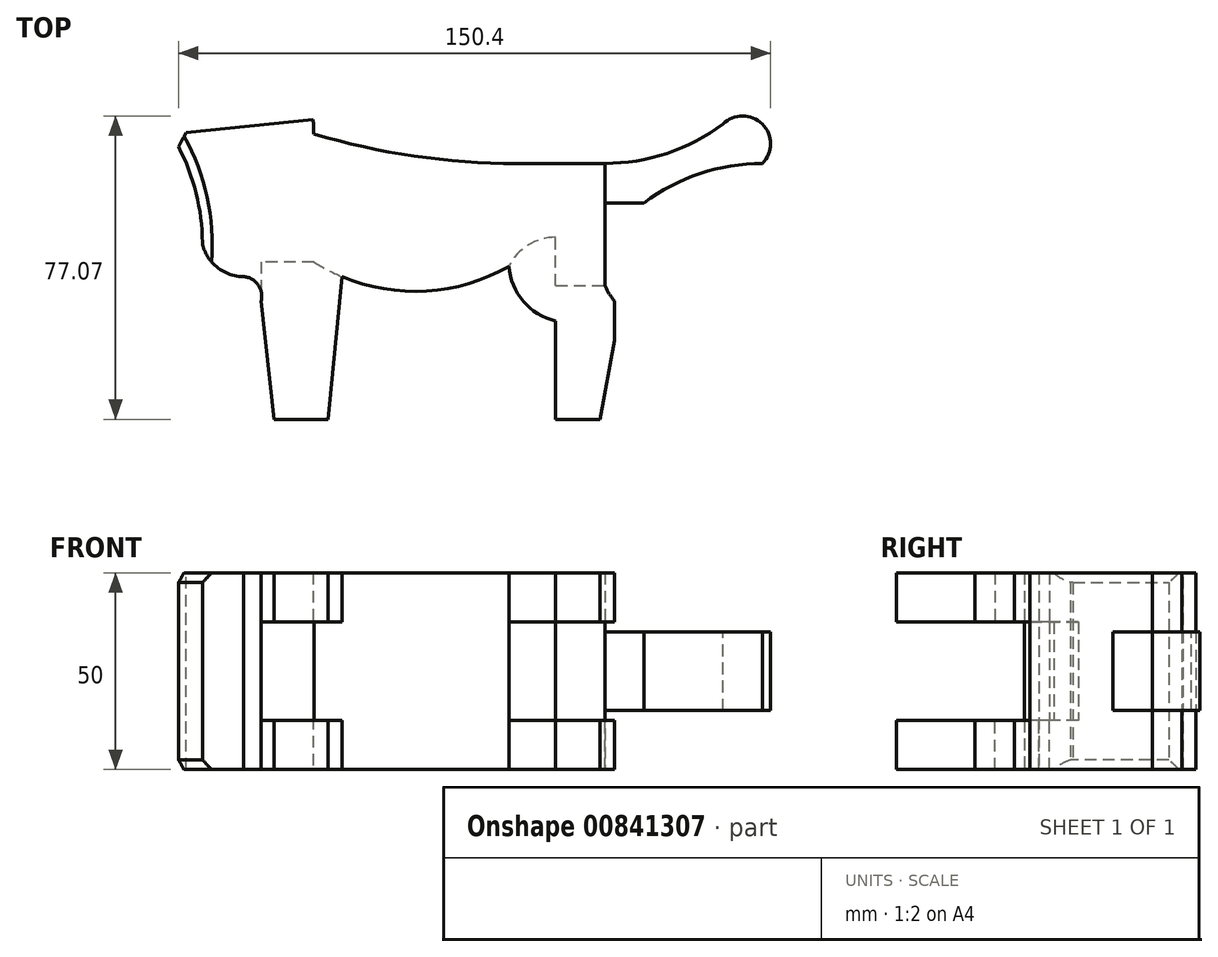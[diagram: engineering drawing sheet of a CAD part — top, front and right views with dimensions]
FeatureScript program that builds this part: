
annotation { "Feature Type Name" : "Feature", "Feature Type Description" : "" }
export const myFeature = defineFeature(function(context is Context, id is Id, definition is map)
    precondition{}
    {
        {
            var Q0;
            Q0=qCreatedBy(makeId("Top.planeOp"),FACE);
            var sketch = newSketch(context, id + "F0", { "sketchPlane" : qUnion([Q0])});
            skLineSegment(sketch, "E0.bottom", {"start": v(-56.24, 60.08) * mm, "end": v(-42.86, 60.08) * mm, "construction": true});
            skLineSegment(sketch, "E0.top", {"start": v(-56.24, 20.08) * mm, "end": v(-49.55, 20.08) * mm, "construction": true});
            skLineSegment(sketch, "E0.left", {"start": v(-56.24, 60.08) * mm, "end": v(-56.24, 27.58) * mm, "construction": true});
            skLineSegment(sketch, "E1", {"start": v(-42.86, 60.08) * mm, "end": v(-42.86, 27.58) * mm, "construction": true});
            skLineSegment(sketch, "E2", {"start": v(8.57, 60.08) * mm, "end": v(8.57, 52.58) * mm, "construction": true});
            skPoint(sketch, "E3", {"position": v(8.57, 52.58) * mm});
            skLineSegment(sketch, "E4", {"start": v(8.57, 52.58) * mm, "end": v(-42.86, 52.58) * mm, "construction": true});
            skArc(sketch, "E5", {"start": v(-42.86, 60.08) * mm, "mid": v(-17.42, 54.46) * mm, "end": v(8.57, 52.58) * mm});
            skPoint(sketch, "E6", {"position": v(8.57, 27.58) * mm});
            skArc(sketch, "E7", {"start": v(-42.86, 27.58) * mm, "mid": v(-17.15, 20.08) * mm, "end": v(8.57, 27.58) * mm});
            skPoint(sketch, "E8", {"position": v(-17.15, 20.08) * mm});
            skLineSegment(sketch, "E9.bottom", {"start": v(8.57, 52.58) * mm, "end": v(18.57, 52.58) * mm});
            skLineSegment(sketch, "E9.top", {"start": v(8.57, 27.58) * mm, "end": v(18.57, 27.58) * mm, "construction": true});
            skLineSegment(sketch, "E9.left", {"start": v(8.57, 52.58) * mm, "end": v(8.57, 27.58) * mm, "construction": true});
            skLineSegment(sketch, "E9.right", {"start": v(18.57, 52.58) * mm, "end": v(18.57, 40.08) * mm});
            skPoint(sketch, "E10", {"position": v(18.57, 40.08) * mm});
            skLineSegment(sketch, "E11", {"start": v(18.57, 40.08) * mm, "end": v(58.57, 40.08) * mm, "construction": true});
            skLineSegment(sketch, "E12", {"start": v(18.57, 52.58) * mm, "end": v(58.57, 52.58) * mm, "construction": true});
            skPoint(sketch, "E13", {"position": v(58.57, 60.08) * mm});
            skLineSegment(sketch, "E14", {"start": v(8.57, 27.58) * mm, "end": v(8.57, 20.08) * mm, "construction": true});
            skLineSegment(sketch, "E15.top", {"start": v(8.57, -12.42) * mm, "end": v(18.57, -12.42) * mm, "construction": true});
            skLineSegment(sketch, "E15.left", {"start": v(8.57, 27.58) * mm, "end": v(8.57, -12.42) * mm, "construction": true});
            skLineSegment(sketch, "E15.right", {"start": v(33.57, 27.58) * mm, "end": v(33.57, 17.58) * mm, "construction": true});
            skLineSegment(sketch, "E16", {"start": v(33.57, 7.58) * mm, "end": v(33.57, -12.42) * mm, "construction": true});
            skLineSegment(sketch, "E17", {"start": v(18.57, 40.08) * mm, "end": v(18.57, 33.83) * mm});
            skLineSegment(sketch, "E18", {"start": v(18.57, 27.58) * mm, "end": v(18.57, 27.58) * mm});
            skLineSegment(sketch, "E19", {"start": v(18.57, 27.58) * mm, "end": v(26.07, 27.58) * mm, "construction": true});
            skLineSegment(sketch, "E20", {"start": v(26.07, 27.58) * mm, "end": v(33.57, 27.58) * mm, "construction": true});
            skArc(sketch, "E21", {"start": v(29.82, 27.58) * mm, "mid": v(25, 32.16) * mm, "end": v(18.57, 33.83) * mm});
            skLineSegment(sketch, "E22", {"start": v(18.57, 27.58) * mm, "end": v(18.57, 12.58) * mm, "construction": true});
            skLineSegment(sketch, "E23", {"start": v(29.82, 27.58) * mm, "end": v(29.82, -12.42) * mm, "construction": true});
            skArc(sketch, "E24", {"start": v(29.82, 27.58) * mm, "mid": v(30.8, 22.24) * mm, "end": v(33.57, 17.58) * mm});
            skLineSegment(sketch, "E25", {"start": v(33.57, 17.58) * mm, "end": v(33.57, 7.58) * mm});
            skLineSegment(sketch, "E26", {"start": v(29.82, -12.42) * mm, "end": v(33.57, 7.58) * mm});
            skPoint(sketch, "E27.orphan", {"position": v(18.57, 33.83) * mm});
            skLineSegment(sketch, "E28", {"start": v(18.57, 33.83) * mm, "end": v(18.57, 27.58) * mm, "construction": true});
            skArc(sketch, "E29", {"start": v(18.57, 33.83) * mm, "mid": v(11.57, 31.83) * mm, "end": v(6.69, 26.44) * mm});
            skLineSegment(sketch, "E30", {"start": v(33.57, 12.58) * mm, "end": v(8.57, 12.58) * mm, "construction": true});
            skArc(sketch, "E31", {"start": v(6.69, 26.44) * mm, "mid": v(10.35, 17.56) * mm, "end": v(18.57, 12.58) * mm});
            skLineSegment(sketch, "E32", {"start": v(18.57, -12.42) * mm, "end": v(33.57, -12.42) * mm});
            skLineSegment(sketch, "E33", {"start": v(18.57, 12.58) * mm, "end": v(18.57, -12.42) * mm});
            skLineSegment(sketch, "E34", {"start": v(-42.86, 27.58) * mm, "end": v(-42.86, 20.08) * mm});
            skLineSegment(sketch, "E35", {"start": v(-42.86, 23.83) * mm, "end": v(-35.71, 23.83) * mm, "construction": true});
            skPoint(sketch, "E36.oppositeSnap0", {"position": v(13.57, -12.42) * mm});
            skLineSegment(sketch, "E36.bottom", {"start": v(-35.71, 23.83) * mm, "end": v(-60.71, 23.83) * mm, "construction": true});
            skLineSegment(sketch, "E36.top", {"start": v(-35.71, -12.42) * mm, "end": v(-39.29, -12.42) * mm, "construction": true});
            skLineSegment(sketch, "E36.left", {"start": v(-35.71, 23.83) * mm, "end": v(-35.71, -12.42) * mm, "construction": true});
            skLineSegment(sketch, "E36.right", {"start": v(-60.71, 23.83) * mm, "end": v(-60.71, -12.42) * mm, "construction": true});
            skLineSegment(sketch, "E37", {"start": v(-35.71, 23.83) * mm, "end": v(-39.29, -12.42) * mm});
            skPoint(sketch, "E37.endSnap0", {"position": v(-39.29, 23.83) * mm});
            skArc(sketch, "E38", {"start": v(-71.18, 32.16) * mm, "mid": v(-67.4, 26.17) * mm, "end": v(-60.71, 23.83) * mm});
            skPoint(sketch, "E38.startSnap0", {"position": v(25, 32.16) * mm});
            skArc(sketch, "E39", {"start": v(-56.24, 17.58) * mm, "mid": v(-57.02, 21.75) * mm, "end": v(-60.71, 23.83) * mm});
            skLineSegment(sketch, "E40", {"start": v(-49.55, 20.08) * mm, "end": v(-42.86, 20.08) * mm, "construction": true});
            skLineSegment(sketch, "E41", {"start": v(-56.24, 17.58) * mm, "end": v(-52.9, -12.42) * mm});
            skPoint(sketch, "E41.endSnap0", {"position": v(-52.9, 20.08) * mm});
            skLineSegment(sketch, "E42", {"start": v(-52.9, -12.42) * mm, "end": v(-60.71, -12.42) * mm, "construction": true});
            skLineSegment(sketch, "E43", {"start": v(-39.29, -12.42) * mm, "end": v(-52.9, -12.42) * mm});
            skLineSegment(sketch, "E44", {"start": v(-71.18, 32.16) * mm, "end": v(-71.18, 60.08) * mm, "construction": true});
            skArc(sketch, "E45", {"start": v(-71.18, 32.16) * mm, "mid": v(-73.2, 46.67) * mm, "end": v(-79.13, 60.08) * mm});
            skLineSegment(sketch, "E46.bottom", {"start": v(-42.86, 60.08) * mm, "end": v(-96.35, 60.08) * mm});
            skLineSegment(sketch, "E46.top", {"start": v(-42.86, 78.17) * mm, "end": v(-96.35, 78.17) * mm});
            skLineSegment(sketch, "E46.left", {"start": v(-42.86, 60.08) * mm, "end": v(-42.86, 78.17) * mm});
            skLineSegment(sketch, "E46.right", {"start": v(-96.35, 60.08) * mm, "end": v(-96.35, 78.17) * mm});
            skLineSegment(sketch, "E47", {"start": v(-42.86, 27.58) * mm, "end": v(-56.24, 27.58) * mm});
            skLineSegment(sketch, "E48", {"start": v(-56.24, 27.58) * mm, "end": v(-56.24, 20.08) * mm});
            skSolve(sketch);
        }
        {
            var Q0;
            {var subQ2=sQuery(id+"F0.wireOp",EDGE,"E5");Q0=makeQuery(id+"F0.imprint","IMPRINT",FACE,{"disambiguationData":[TD([[makeQuery(id+"F0.imprint","IMPRINT",EDGE,{"derivedFrom":subQ2}),-1.0]])]});}
            var Q1;
            {var subQ1=sQuery(id+"F0.wireOp",EDGE,"E37");Q1=makeQuery(id+"F0.imprint","IMPRINT",FACE,{"disambiguationData":[TD([[makeQuery(id+"F0.imprint","IMPRINT",EDGE,{"derivedFrom":subQ1}),-1.0]])]});}
            var Q2;
            Q2=makeQuery(id+"F0.imprint","IMPRINT",FACE,{"disambiguationData":[TD([[makeQuery(id+"F0.imprint","IMPRINT",EDGE,{"derivedFrom":sQuery(id+"F0.wireOp",EDGE,"E21")}),1.0]])]});
            extrude(context, id + "F1", {"entities" : qUnion([Q0, Q1, Q2]), "depth" : 25 * mm, "offsetDistance" : 25 * mm});
        }
        {
            var Q0;
            Q0=makeQuery(id+"F0.imprint","IMPRINT",FACE,{"disambiguationData":[TD([[makeQuery(id+"F0.imprint","IMPRINT",EDGE,{"derivedFrom":sQuery(id+"F0.wireOp",EDGE,"E21")}),1.0]])]});
            var Q1;
            {var subQ1=sQuery(id+"F0.wireOp",EDGE,"E37");Q1=makeQuery(id+"F0.imprint","IMPRINT",FACE,{"disambiguationData":[TD([[makeQuery(id+"F0.imprint","IMPRINT",EDGE,{"derivedFrom":subQ1}),-1.0]])]});}
            extrude(context, id + "F2", {"entities" : qUnion([Q0, Q1]), "operationType" : NewBodyOperationType.REMOVE, "depth" : 12.5 * mm, "offsetDistance" : 25 * mm});
        }
        {
            var Q0;
            Q0=makeQuery(id+"F1.opExtrude","SWEPT_BODY",BODY,{"disambiguationData":[OSD([sQuery(id+"F0.wireOp",EDGE,"E5"),sQuery(id+"F0.wireOp",EDGE,"E7"),sQuery(id+"F0.wireOp",EDGE,"E9.bottom"),sQuery(id+"F0.wireOp",EDGE,"E9.right"),sQuery(id+"F0.wireOp",EDGE,"E17"),sQuery(id+"F0.wireOp",EDGE,"E21"),sQuery(id+"F0.wireOp",EDGE,"E24"),sQuery(id+"F0.wireOp",EDGE,"E25"),sQuery(id+"F0.wireOp",EDGE,"E26"),sQuery(id+"F0.wireOp",EDGE,"E31"),sQuery(id+"F0.wireOp",EDGE,"E32"),sQuery(id+"F0.wireOp",EDGE,"E33"),sQuery(id+"F0.wireOp",EDGE,"E37"),sQuery(id+"F0.wireOp",EDGE,"E38"),sQuery(id+"F0.wireOp",EDGE,"E39"),sQuery(id+"F0.wireOp",EDGE,"E41"),sQuery(id+"F0.wireOp",EDGE,"E43"),sQuery(id+"F0.wireOp",EDGE,"E45"),sQuery(id+"F0.wireOp",EDGE,"E46.bottom")])]});
            var Q1;
            Q1=qCreatedBy(makeId("Top.planeOp"),FACE);
            mirror(context, id + "F3", {"operationType" : NewBodyOperationType.ADD, "entities" : qUnion([Q0]), "mirrorPlane" : qUnion([Q1])});
        }
        {
            var Q0;
            {var subQ0=makeQuery(id+"F1.opExtrude","SWEPT_FACE",FACE,{"disambiguationData":[OSD([sQuery(id+"F0.wireOp",EDGE,"E9.right"),sQuery(id+"F0.wireOp",EDGE,"E17")])]});Q0=makeQuery(id+"F3.boolean.opBoolean","MERGE",FACE,{"derivedFrom":[subQ0,makeQuery(id+"F3.opPattern","COPY",FACE,{"derivedFrom":subQ0,"instanceName":"1"})]});}
            extrude(context, id + "F4", {"entities" : qUnion([Q0]), "operationType" : NewBodyOperationType.ADD, "depth" : 12.5 * mm, "offsetDistance" : 25 * mm});
        }
        {
            var Q0;
            Q0=makeQuery(id+"F4.opExtrude","SWEPT_FACE",FACE,{"disambiguationData":[OSD([sQuery(id+"F0.wireOp",EDGE,"E17"),sQuery(id+"F0.wireOp",EDGE,"E21"),sQuery(id+"F0.wireOp",EDGE,"E29")])]});
            var Q1;
            Q1=makeQuery(id+"F1.opExtrude","CAP_VERTEX",VERTEX,{"disambiguationData":[OSD([sQuery(id+"F0.wireOp",EDGE,"E24"),sQuery(id+"F0.wireOp",EDGE,"E25")])],"isStart":false});
            extrude(context, id + "F5", {"entities" : qUnion([Q0]), "operationType" : NewBodyOperationType.ADD, "endBound" : BoundingType.UP_TO_VERTEX, "depth" : 25 * mm, "endBoundEntityVertex" : qUnion([Q1]), "offsetDistance" : 25 * mm});
        }
        {
            var Q0;
            {var subQ0=sQuery(id+"F0.wireOp",EDGE,"E29");var subQ1=sQuery(id+"F0.wireOp",EDGE,"E21");var subQ2=sQuery(id+"F0.wireOp",EDGE,"E17");Q0=makeQuery(id+"F5.boolean.opBoolean","MERGE",FACE,{"derivedFrom":[makeQuery(id+"F4.opExtrude","CAP_FACE",FACE,{"disambiguationData":[OSD([sQuery(id+"F0.wireOp",EDGE,"E9.right"),subQ2])],"isStart":false}),makeQuery(id+"F5.opExtrude","SWEPT_FACE",FACE,{"disambiguationData":[OSD([subQ2,subQ1,subQ0]),TDD([makeQuery(id+"F4.opExtrude","CAP_EDGE",EDGE,{"disambiguationData":[OSD([subQ2,subQ1,subQ0])],"isStart":false})])]})]});}
            var sketch = newSketch(context, id + "F6", { "sketchPlane" : qUnion([Q0])});
            skLineSegment(sketch, "E49.0.0", {"start": v(52.58, 25) * mm, "end": v(21.54, 25) * mm});
            skLineSegment(sketch, "E49.0.1", {"start": v(21.54, 25) * mm, "end": v(21.54, 12.5) * mm});
            skLineSegment(sketch, "E49.0.2", {"start": v(21.54, 12.5) * mm, "end": v(17.58, 12.5) * mm});
            skLineSegment(sketch, "E49.0.3", {"start": v(17.58, 12.5) * mm, "end": v(17.58, -12.5) * mm});
            skLineSegment(sketch, "E49.0.4", {"start": v(17.58, -12.5) * mm, "end": v(21.54, -12.5) * mm});
            skLineSegment(sketch, "E49.0.5", {"start": v(21.54, -12.5) * mm, "end": v(21.54, -25) * mm});
            skLineSegment(sketch, "E49.0.6", {"start": v(21.54, -25) * mm, "end": v(52.58, -25) * mm});
            skLineSegment(sketch, "E49.0.7", {"start": v(52.58, -25) * mm, "end": v(52.58, 25) * mm});
            skLineSegment(sketch, "E50", {"start": v(21.54, 12.5) * mm, "end": v(21.54, -12.5) * mm});
            skArc(sketch, "E51", {"start": v(52.58, 12.5) * mm, "mid": v(37.06, 25) * mm, "end": v(21.54, 12.5) * mm});
            skPoint(sketch, "E52", {"position": v(37.06, 25) * mm});
            skLineSegment(sketch, "E53", {"start": v(52.58, 0) * mm, "end": v(21.54, 0) * mm});
            skLineSegment(sketch, "E54.bottom", {"start": v(62.58, -10) * mm, "end": v(42.58, -10) * mm});
            skLineSegment(sketch, "E54.top", {"start": v(62.58, 10) * mm, "end": v(42.58, 10) * mm});
            skLineSegment(sketch, "E54.left", {"start": v(62.58, -10) * mm, "end": v(62.58, 10) * mm});
            skLineSegment(sketch, "E54.right", {"start": v(42.58, -10) * mm, "end": v(42.58, 10) * mm});
            skPoint(sketch, "E54.middle", {"position": v(52.58, 0) * mm});
            skSolve(sketch);
        }
        {
            var Q0;
            Q0=makeQuery(id+"F6.imprint","IMPRINT",FACE,{"disambiguationData":[TD([[makeQuery(id+"F6.imprint","IMPRINT",EDGE,{"derivedFrom":sQuery(id+"F6.wireOp",EDGE,"E49.0.2")}),-1.0]])]});
            var Q1;
            Q1=makeQuery(id+"F1.opExtrude","CAP_VERTEX",VERTEX,{"disambiguationData":[OSD([sQuery(id+"F0.wireOp",EDGE,"E7"),sQuery(id+"F0.wireOp",EDGE,"E29"),sQuery(id+"F0.wireOp",EDGE,"E31")])],"isStart":false});
            extrude(context, id + "F7", {"entities" : qUnion([Q0]), "operationType" : NewBodyOperationType.REMOVE, "endBound" : BoundingType.UP_TO_VERTEX, "oppositeDirection" : true, "depth" : 25 * mm, "endBoundEntityVertex" : qUnion([Q1]), "offsetDistance" : 25 * mm});
        }
        {
            var Q0;
            {var subQ0=sQuery(id+"F6.wireOp",EDGE,"E54.left");Q0=makeQuery(id+"F6.imprint","IMPRINT",FACE,{"disambiguationData":[TD([[makeQuery(id+"F6.imprint","IMPRINT",EDGE,{"derivedFrom":subQ0}),1.0]])]});}
            var Q1;
            {var subQ0=sQuery(id+"F6.wireOp",EDGE,"E53");var subQ1=sQuery(id+"F6.wireOp",EDGE,"E49.0.7");var subQ2=makeQuery(id+"F6.imprint","INTERSECT",VERTEX,{"derivedFrom":[subQ1,subQ0]});Q1=makeQuery(id+"F6.imprint","IMPRINT",FACE,{"disambiguationData":[TD([[makeQuery(id+"F6.imprint","IMPRINT",EDGE,{"disambiguationData":[TD([[subQ2,-1.0]])],"derivedFrom":subQ1}),-1.0]])]});}
            var Q2;
            {var subQ0=sQuery(id+"F6.wireOp",EDGE,"E53");var subQ1=sQuery(id+"F6.wireOp",EDGE,"E49.0.7");var subQ2=makeQuery(id+"F6.imprint","INTERSECT",VERTEX,{"derivedFrom":[subQ1,subQ0]});Q2=makeQuery(id+"F6.imprint","IMPRINT",FACE,{"disambiguationData":[TD([[makeQuery(id+"F6.imprint","IMPRINT",EDGE,{"disambiguationData":[TD([[subQ2,1.0]])],"derivedFrom":subQ1}),-1.0]])]});}
            extrude(context, id + "F8", {"entities" : qUnion([Q0, Q1, Q2]), "operationType" : NewBodyOperationType.ADD, "depth" : 40 * mm, "offsetDistance" : 25 * mm});
        }
        {
            var Q0;
            Q0=makeQuery(id+"F8.opExtrude","SWEPT_FACE",FACE,{"disambiguationData":[OSD([sQuery(id+"F6.wireOp",EDGE,"E54.top")])]});
            var sketch = newSketch(context, id + "F9", { "sketchPlane" : qUnion([Q0])});
            skLineSegment(sketch, "E55.0", {"start": v(71.07, 62.58) * mm, "end": v(51.07, 62.58) * mm});
            skLineSegment(sketch, "E56.0", {"start": v(31.07, 62.58) * mm, "end": v(31.07, 42.58) * mm});
            skPoint(sketch, "E57.0", {"position": v(31.07, 42.58) * mm});
            skLineSegment(sketch, "E58.0", {"start": v(71.07, 42.58) * mm, "end": v(51.07, 42.58) * mm});
            skLineSegment(sketch, "E59.0", {"start": v(71.07, 62.58) * mm, "end": v(71.07, 42.58) * mm});
            skLineSegment(sketch, "E60.0", {"start": v(31.07, 52.58) * mm, "end": v(31.07, 21.54) * mm});
            skLineSegment(sketch, "E61", {"start": v(51.07, 62.58) * mm, "end": v(31.07, 62.58) * mm});
            skLineSegment(sketch, "E62", {"start": v(51.07, 42.58) * mm, "end": v(31.07, 42.58) * mm});
            skLineSegment(sketch, "E63", {"start": v(31.07, 52.58) * mm, "end": v(71.07, 52.58) * mm, "construction": true});
            skArc(sketch, "E64", {"start": v(31.07, 52.58) * mm, "mid": v(46.88, 55.14) * mm, "end": v(61.07, 62.58) * mm});
            skLineSegment(sketch, "E65", {"start": v(31.07, 42.58) * mm, "end": v(71.07, 62.58) * mm, "construction": true});
            skArc(sketch, "E66", {"start": v(71.07, 52.58) * mm, "mid": v(55.26, 50.01) * mm, "end": v(41.07, 42.58) * mm});
            skLineSegment(sketch, "E67", {"start": v(61.07, 62.58) * mm, "end": v(71.07, 52.58) * mm});
            skSolve(sketch);
        }
        {
            var Q0;
            Q0=makeQuery(id+"F9.imprint","IMPRINT",FACE,{"disambiguationData":[TD([[makeQuery(id+"F9.imprint","IMPRINT",EDGE,{"derivedFrom":sQuery(id+"F9.wireOp",EDGE,"E56.0")}),1.0]])]});
            var Q1;
            {var subQ3=sQuery(id+"F9.wireOp",EDGE,"E67");Q1=makeQuery(id+"F9.imprint","IMPRINT",FACE,{"disambiguationData":[TD([[makeQuery(id+"F9.imprint","IMPRINT",EDGE,{"derivedFrom":subQ3}),1.0]])]});}
            var Q2;
            {var subQ0=sQuery(id+"F9.wireOp",EDGE,"E58.0");Q2=makeQuery(id+"F9.imprint","IMPRINT",FACE,{"disambiguationData":[TD([[makeQuery(id+"F9.imprint","IMPRINT",EDGE,{"derivedFrom":subQ0}),-1.0]])]});}
            var Q3;
            Q3=makeQuery(id+"F8.opExtrude","SWEPT_FACE",FACE,{"disambiguationData":[OSD([sQuery(id+"F6.wireOp",EDGE,"E54.bottom")])]});
            extrude(context, id + "F10", {"entities" : qUnion([Q0, Q1, Q2]), "operationType" : NewBodyOperationType.REMOVE, "endBound" : BoundingType.UP_TO_SURFACE, "oppositeDirection" : true, "depth" : 25 * mm, "endBoundEntityFace" : qUnion([Q3]), "offsetDistance" : 25 * mm});
        }
        {
            var Q0;
            Q0=makeQuery(id+"F10.boolean.opBoolean","COPY",FACE,{"derivedFrom":makeQuery(id+"F10.opExtrude","SWEPT_FACE",FACE,{"disambiguationData":[OSD([sQuery(id+"F9.wireOp",EDGE,"E67")])]})});
            var sketch = newSketch(context, id + "F11", { "sketchPlane" : qUnion([Q0])});
            skLineSegment(sketch, "E68", {"start": v(-6, 10) * mm, "end": v(-6, -10) * mm});
            skSolve(sketch);
        }
        {
            var Q0;
            {var subQ0=sQuery(id+"F11.wireOp",EDGE,"E68");Q0=makeQuery(id+"F11.imprint","IMPRINT",FACE,{"disambiguationData":[TD([[makeQuery(id+"F11.imprint","IMPRINT",EDGE,{"derivedFrom":subQ0}),1.0]])]});}
            var Q1;
            Q1=sQuery(id+"F11.wireOp",EDGE,"E68");
            revolve(context, id + "F12", {"operationType" : NewBodyOperationType.ADD, "surfaceOperationType" : NewSurfaceOperationType.NEW, "entities" : qUnion([Q0]), "axis" : qUnion([Q1]), "revolveType" : RevolveType.ONE_DIRECTION, "angle" : (PI) * radian});
        }
        {
            var Q0;
            {var subQ0=makeQuery(id+"F1.opExtrude","SWEPT_FACE",FACE,{"disambiguationData":[OSD([sQuery(id+"F0.wireOp",EDGE,"E46.bottom")])]});Q0=makeQuery(id+"F3.boolean.opBoolean","MERGE",FACE,{"derivedFrom":[subQ0,makeQuery(id+"F3.opPattern","COPY",FACE,{"derivedFrom":subQ0,"instanceName":"1"})]});}
            var sketch = newSketch(context, id + "F13", { "sketchPlane" : qUnion([Q0])});
            skLineSegment(sketch, "E69.0", {"start": v(42.86, -25) * mm, "end": v(79.13, -25) * mm});
            skLineSegment(sketch, "E70.0", {"start": v(42.86, 25) * mm, "end": v(79.13, 25) * mm});
            skLineSegment(sketch, "E71.0", {"start": v(79.13, 25) * mm, "end": v(79.13, -25) * mm});
            skPoint(sketch, "E72", {"position": v(92.83, 25) * mm});
            skLineSegment(sketch, "E73", {"start": v(92.83, 25) * mm, "end": v(92.83, -25) * mm});
            skPoint(sketch, "E74", {"position": v(67.86, -25) * mm});
            skLineSegment(sketch, "E75", {"start": v(67.86, -25) * mm, "end": v(67.86, 25) * mm});
            skSolve(sketch);
        }
        {
            var Q0;
            {var subQ3=sQuery(id+"F13.wireOp",EDGE,"E75");Q0=makeQuery(id+"F13.imprint","IMPRINT",FACE,{"disambiguationData":[TD([[makeQuery(id+"F13.imprint","IMPRINT",EDGE,{"derivedFrom":subQ3}),1.0]])]});}
            var Q1;
            {var subQ0=sQuery(id+"F13.wireOp",EDGE,"E71.0");Q1=makeQuery(id+"F13.imprint","IMPRINT",FACE,{"disambiguationData":[TD([[makeQuery(id+"F13.imprint","IMPRINT",EDGE,{"derivedFrom":subQ0}),-1.0]])]});}
            var Q2;
            Q2=sQuery(id+"F13.wireOp",EDGE,"E71.0");
            revolve(context, id + "F14", {"operationType" : NewBodyOperationType.ADD, "surfaceOperationType" : NewSurfaceOperationType.NEW, "entities" : qUnion([Q0, Q1]), "axis" : qUnion([Q2]), "revolveType" : RevolveType.ONE_DIRECTION, "oppositeDirection" : true, "angle" : .1 * radian});
        }
        {
            var Q0;
            {var subQ0=makeQuery(id+"F1.opExtrude","SWEPT_FACE",FACE,{"disambiguationData":[OSD([sQuery(id+"F0.wireOp",EDGE,"E45")])]});Q0=makeQuery(id+"F3.boolean.opBoolean","MERGE",FACE,{"derivedFrom":[subQ0,makeQuery(id+"F3.opPattern","COPY",FACE,{"derivedFrom":subQ0,"instanceName":"1"})]});}
            chamfer(context, id + "F15", {"entities" : qUnion([Q0]), "width" : 2.5 * mm, "tangentPropagation" : true});
        }
    });
